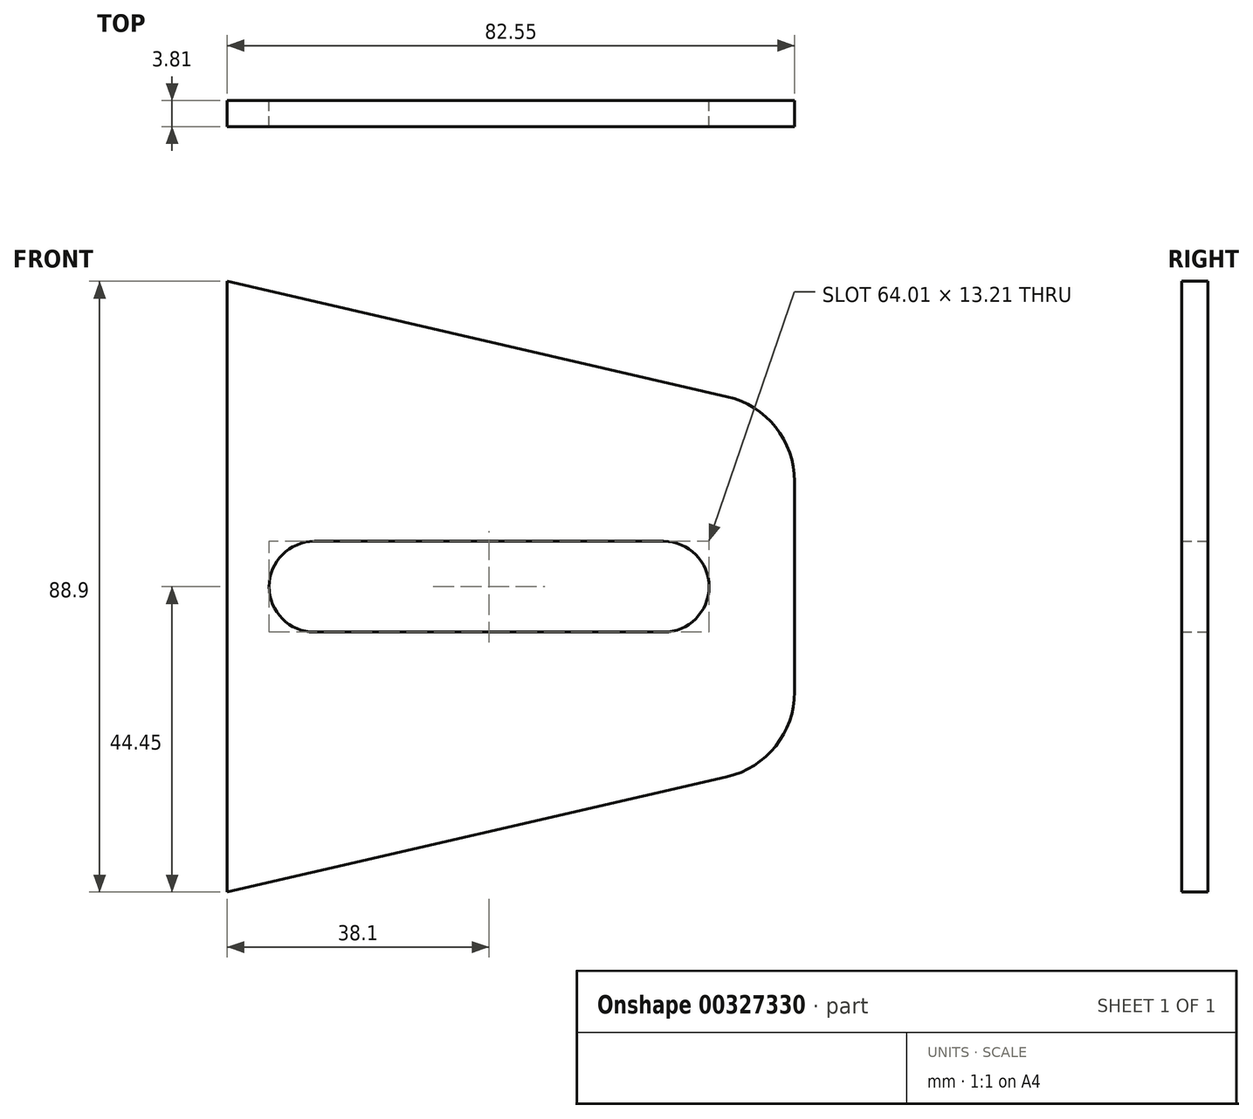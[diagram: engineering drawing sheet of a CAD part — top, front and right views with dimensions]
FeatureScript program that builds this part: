
annotation { "Feature Type Name" : "Feature", "Feature Type Description" : "" }
export const myFeature = defineFeature(function(context is Context, id is Id, definition is map)
    precondition{}
    {
        {
            var Q0;
            Q0=qCreatedBy(makeId("Front.planeOp"),FACE);
            var sketch = newSketch(context, id + "F0", { "sketchPlane" : qUnion([Q0])});
            skLineSegment(sketch, "E0", {"start": v(0, 44.45) * mm, "end": v(0, -44.45) * mm});
            skLineSegment(sketch, "E1", {"start": v(0, -44.45) * mm, "end": v(82.55, -25.4) * mm});
            skLineSegment(sketch, "E2", {"start": v(82.55, -25.4) * mm, "end": v(82.55, 25.4) * mm});
            skLineSegment(sketch, "E3", {"start": v(82.55, 25.4) * mm, "end": v(0, 44.45) * mm});
            skArc(sketch, "E4", {"start": v(12.7, 6.6) * mm, "mid": v(6.1, 0) * mm, "end": v(12.7, -6.6) * mm});
            skArc(sketch, "E5", {"start": v(63.5, -6.6) * mm, "mid": v(70.1, 0) * mm, "end": v(63.5, 6.6) * mm});
            skLineSegment(sketch, "E6.bottom", {"start": v(12.7, 6.6) * mm, "end": v(63.5, 6.6) * mm});
            skLineSegment(sketch, "E6.top", {"start": v(12.7, -6.6) * mm, "end": v(63.5, -6.6) * mm});
            skSolve(sketch);
        }
        {
            var Q0;
            Q0 = qSketchRegion(id + "F0", true);
            extrude(context, id + "F1", {"entities" : qUnion([Q0]), "depth" : 3.8 * mm});
        }
        {
            var Q0;
            Q0=makeQuery(id+"F1.opExtrude","SWEPT_EDGE",EDGE,{"disambiguationData":[OSD([sQuery(id+"F0.wireOp",EDGE,"E2"),sQuery(id+"F0.wireOp",EDGE,"E3")])]});
            var Q1;
            Q1=makeQuery(id+"F1.opExtrude","SWEPT_EDGE",EDGE,{"disambiguationData":[OSD([sQuery(id+"F0.wireOp",EDGE,"E1"),sQuery(id+"F0.wireOp",EDGE,"E2")])]});
            fillet(context, id + "F2", {"entities" : qUnion([Q0, Q1]), "radius" : 12.7 * mm, "tangentPropagation" : true, "allowEdgeOverflow" : false});
        }
    });
